# Revit family: Hager-UNIVERS-Surface_mounted-IP44-With_Cover-With_DIN-Hosted-PL-pl
name_source: partatom
category: Electrical Equipment
units: mm (PartAtom-declared; Revit-internal decimal feet)

## family parameters
Cut with Voids When Loaded = No
Host = Face
Maintain Annotation Orientation = Yes
Panel Configuration = Two Columns, Circuits Across
Part Type = Panelboard
Room Calculation Point = No
Round Connector Dimension = Use Diameter
Shared = No

## types (33) — shared parameters
BC_MODEL_ID = 1546917
BC_OBJECT_ID = 513407
BC_OBJECT_VERSION = #12
Code hager = ADD-EC000214_EU
EF000007 - Kolor = Biały
EF000024 - Odporność na promieniowanie UV = No
EF000049 - Głębokość = 165 mm  [stored 0.541339 ft]
EF000116 - Numer RAL = 9010
EF000118 - Z płytą montażową = No
EF000218 - Głębokość wbudowania = 161 mm  [stored 0.528215 ft]
EF001062 - Wykonanie zgodne z Dyrektywą Kompatybilności Elektromagnetycznej EMC = No
EF001088 - Możliwość rozbudowy = Yes
EF001134 - Szyna DIN = Yes
EF004462 - Rodzaj zamknięcia = Inne
EF005474 - Stopień ochrony (IP) = IP44
EF006244 - Transparentna pokrywa/drzwi = No
EF006306 - Z zamkiem = No
EF015941 - Drzwi przepuszczające sygnał = No
ETIM class code = EC000214
ETIM class name = Small distribution board
HG000002-with door or cover-pl = Yes
HG000003-Range-pl = UNIVERS
HG000005-Thickness-pl = 2 mm  [stored 0.00656168 ft]
HG000006-Flush mounted-pl = No
HG000011-Empty rows from bottom-pl = No
HG000012-Door swing angle-pl = 90.00°
HG000013-Door on the left-pl = No
HG000014-Door on the right-pl = Yes
HG000015-Clearance visibility-pl = Yes
HG000016-Door 3D visibility-pl = Yes
HG000017-Distance between poles-pl = 18 mm  [stored 0.0590551 ft]
HG000060-RAL-number = 9010
HG000099-Onfly Template ID-pl-PL = 507532
Manufacturer = Hager
Name = Hager-UNIVERS-Surface_mounted-IP44-With_Cover-With_DIN-NoHosted-PL-pl
Name BIM&CO = Electricity
Name hager = ADD_Enclosures_EC000214
Uniformat = Low Tension Service & Dist.
Uniformat code = D501001
zero-valued in all types: Default Elevation, EF001131 - Głębokość wewnętrzna, HG000007-Number of empty columns-pl

## per-type parameters (varying)
| type | BC_VARIANT_ID | EF000003 - Sposób montażu | EF000008 - Szerokość | EF000040 - Wysokość | EF000266 - Liczba rzędów | EF000332 - Wysokość wbudowania | EF000846 - Szerokość wbudowania | EF002950 - Szerokość wyrażona liczbą modułów | EF009212 - Wykonanie/rodzaj pokrywy | EF015776 - Listwa zaciskowa uziemienia | EF015777 - Listwa zaciskowa przewodu neutralnego | HG000001-Number of columns-pl | HG000004-Manufacturer reference-pl | HG000008-Number of empty rows-pl | HG000009-Double swing door-pl | HG000010-Asymmetric doors-pl | HGEF000266-Liczba rzędów | HGEF0002950-Szerokość wyrażona liczbą modułów |
| UNIVERS-Surface_mounted_W300_H500_D165_12_Modular_Spacing-FWB31S | 1173306 | Montaż natynkowy | 300 mm | 500 mm  [stored 1.64042 ft] | 3 | 500 mm  [stored 1.64042 ft] | 300 mm | 12 | Z otworem | Yes | Yes | 1 | FWB31S | 0 | No | No | 3 | 12 |
| UNIVERS-Surface_mounted_W550_H500_D165_26_Modular_Spacing-FWB32M2 | 1173307 | Montaż natynkowy | 550 mm | 500 mm  [stored 1.64042 ft] | 3 | 500 mm  [stored 1.64042 ft] | 550 mm | 26 | Zamknięty | No | No | 1 | FWB32M2 | 0 | No | No | 3 | 26 |
| UNIVERS-Surface_mounted_W550_H500_D165_24_Modular_Spacing-FWB32S | 1173308 | Montaż natynkowy | 550 mm | 500 mm  [stored 1.64042 ft] | 3 | 500 mm  [stored 1.64042 ft] | 550 mm | 24 | Z otworem | Yes | Yes | 2 | FWB32S | 0 | No | No | 3 | 24 |
| UNIVERS-Surface_mounted_W800_H500_D165_36_Modular_Spacing-FWB33S | 1173309 | Montaż natynkowy | 800 mm  [stored 2.62467 ft] | 500 mm  [stored 1.64042 ft] | 3 | 500 mm  [stored 1.64042 ft] | 800 mm  [stored 2.62467 ft] | 36 | Z otworem | Yes | Yes | 3 | FWB33S | 0 | Yes | Yes | 3 | 36 |
| UNIVERS-Surface_mounted_W1050_H500_D165_48_Modular_Spacing-FWB34S | 1173310 | Montaż natynkowy | 1050 mm | 500 mm  [stored 1.64042 ft] | 3 | 500 mm  [stored 1.64042 ft] | 1050 mm | 48 | Z otworem | Yes | Yes | 4 | FWB34S | 0 | Yes | No | 3 | 48 |
| UNIVERS-Surface_mounted_W300_H650_D165_12_Modular_Spacing-FWB41S | 1173311 | Montaż natynkowy | 300 mm | 650 mm  [stored 2.13255 ft] | 4 | 650 mm  [stored 2.13255 ft] | 300 mm | 12 | Z otworem | Yes | Yes | 1 | FWB41S | 0 | No | No | 4 | 12 |
| UNIVERS-Surface_mounted_W550_H650_D165_26_Modular_Spacing-FWB42M2 | 1173312 | Montaż natynkowy | 550 mm | 650 mm  [stored 2.13255 ft] | 4 | 650 mm  [stored 2.13255 ft] | 550 mm | 26 | Zamknięty | No | No | 1 | FWB42M2 | 0 | No | No | 4 | 26 |
| UNIVERS-Surface_mounted_W550_H650_D165_24_Modular_Spacing-FWB42S | 1173313 | Natynkowy/podtynkowy | 550 mm | 650 mm  [stored 2.13255 ft] | 4 | 650 mm  [stored 2.13255 ft] | 550 mm | 24 | Z otworem | Yes | Yes | 2 | FWB42S | 0 | No | No | 4 | 24 |
| UNIVERS-Surface_mounted_W800_H650_D165_36_Modular_Spacing-FWB43S | 1173314 | Montaż natynkowy | 800 mm  [stored 2.62467 ft] | 650 mm  [stored 2.13255 ft] | 4 | 650 mm  [stored 2.13255 ft] | 800 mm  [stored 2.62467 ft] | 36 | Z otworem | Yes | Yes | 3 | FWB43S | 0 | Yes | Yes | 4 | 36 |
| UNIVERS-Surface_mounted_W1050_H650_D165_48_Modular_Spacing-FWB44S | 1173315 | Montaż natynkowy | 1050 mm | 650 mm  [stored 2.13255 ft] | 4 | 650 mm  [stored 2.13255 ft] | 1050 mm | 48 | Z otworem | Yes | Yes | 4 | FWB44S | 0 | Yes | No | 4 | 48 |
| UNIVERS-Surface_mounted_W300_H800_D165_12_Modular_Spacing-FWB51S | 1173316 | Montaż natynkowy | 300 mm | 800 mm  [stored 2.62467 ft] | 5 | 800 mm  [stored 2.62467 ft] | 300 mm | 12 | Z otworem | Yes | Yes | 1 | FWB51S | 0 | No | No | 5 | 12 |
| UNIVERS-Surface_mounted_W550_H800_D165_26_Modular_Spacing-FWB52M2 | 1173317 | Montaż natynkowy | 550 mm | 800 mm  [stored 2.62467 ft] | 5 | 800 mm  [stored 2.62467 ft] | 550 mm | 26 | Zamknięty | No | No | 1 | FWB52M2 | 0 | No | No | 5 | 26 |
| UNIVERS-Surface_mounted_W550_H800_D165_24_Modular_Spacing-FWB52N | 1173318 | Montaż natynkowy | 550 mm | 800 mm  [stored 2.62467 ft] | 5 | 800 mm  [stored 2.62467 ft] | 550 mm | 24 | Z otworem | No | No | 2 | FWB52N | 2 | No | No | 5 | 24 |
| UNIVERS-Surface_mounted_W550_H800_D165_24_Modular_Spacing-FWB52S | 1173319 | Montaż natynkowy | 550 mm | 800 mm  [stored 2.62467 ft] | 5 | 800 mm  [stored 2.62467 ft] | 550 mm | 24 | Z otworem | Yes | Yes | 2 | FWB52S | 0 | No | No | 5 | 24 |
| UNIVERS-Surface_mounted_W800_H800_D165_36_Modular_Spacing-FWB53N | 1173320 | Montaż natynkowy | 800 mm  [stored 2.62467 ft] | 800 mm  [stored 2.62467 ft] | 5 | 800 mm  [stored 2.62467 ft] | 800 mm  [stored 2.62467 ft] | 36 | Z otworem | No | No | 3 | FWB53N | 2 | Yes | Yes | 5 | 36 |
| UNIVERS-Surface_mounted_W800_H800_D165_36_Modular_Spacing-FWB53S | 1173321 | Montaż natynkowy | 800 mm  [stored 2.62467 ft] | 800 mm  [stored 2.62467 ft] | 5 | 800 mm  [stored 2.62467 ft] | 800 mm  [stored 2.62467 ft] | 36 | Z otworem | Yes | Yes | 3 | FWB53S | 0 | Yes | Yes | 5 | 36 |
| UNIVERS-Surface_mounted_W1050_H800_D165_48_Modular_Spacing-FWB54S | 1173322 | Montaż natynkowy | 1050 mm | 800 mm  [stored 2.62467 ft] | 5 | 800 mm  [stored 2.62467 ft] | 1050 mm | 48 | Z otworem | Yes | Yes | 4 | FWB54S | 0 | Yes | No | 5 | 48 |
| UNIVERS-Surface_mounted_W300_H950_D165_12_Modular_Spacing-FWB61S | 1173323 | Montaż natynkowy | 300 mm | 950 mm  [stored 3.1168 ft] | 6 | 950 mm  [stored 3.1168 ft] | 300 mm | 12 | Z otworem | Yes | Yes | 1 | FWB61S | 0 | No | No | 6 | 12 |
| UNIVERS-Surface_mounted_W550_H950_D165_26_Modular_Spacing-FWB62M2 | 1173324 | Montaż natynkowy | 550 mm | 950 mm  [stored 3.1168 ft] | 6 | 950 mm  [stored 3.1168 ft] | 550 mm | 26 | Zamknięty | No | No | 1 | FWB62M2 | 0 | No | No | 6 | 26 |
| UNIVERS-Surface_mounted_W550_H950_D165_24_Modular_Spacing-FWB62N | 1173325 | Montaż natynkowy | 550 mm | 950 mm  [stored 3.1168 ft] | 6 | 950 mm  [stored 3.1168 ft] | 550 mm | 24 | Z otworem | No | No | 2 | FWB62N | 2 | No | No | 6 | 24 |
| UNIVERS-Surface_mounted_W550_H950_D165_24_Modular_Spacing-FWB62S | 1173326 | Montaż natynkowy | 550 mm | 950 mm  [stored 3.1168 ft] | 6 | 950 mm  [stored 3.1168 ft] | 550 mm | 24 | Z otworem | Yes | Yes | 2 | FWB62S | 0 | No | No | 6 | 24 |
| UNIVERS-Surface_mounted_W800_H950_D165_36_Modular_Spacing-FWB63N | 1173327 | Montaż natynkowy | 800 mm  [stored 2.62467 ft] | 950 mm  [stored 3.1168 ft] | 6 | 950 mm  [stored 3.1168 ft] | 800 mm  [stored 2.62467 ft] | 36 | Z otworem | No | No | 3 | FWB63N | 2 | Yes | Yes | 6 | 36 |
| UNIVERS-Surface_mounted_W800_H950_D165_36_Modular_Spacing-FWB63S | 1173328 | Montaż natynkowy | 800 mm  [stored 2.62467 ft] | 950 mm  [stored 3.1168 ft] | 6 | 950 mm  [stored 3.1168 ft] | 800 mm  [stored 2.62467 ft] | 36 | Z otworem | Yes | Yes | 3 | FWB63S | 0 | Yes | Yes | 6 | 36 |
| UNIVERS-Surface_mounted_W1050_H950_D165_48_Modular_Spacing-FWB64N | 1173329 | Montaż natynkowy | 1050 mm | 950 mm  [stored 3.1168 ft] | 6 | 950 mm  [stored 3.1168 ft] | 1050 mm | 48 | Z otworem | No | No | 4 | FWB64N | 2 | Yes | No | 6 | 48 |
| UNIVERS-Surface_mounted_W1050_H950_D165_48_Modular_Spacing-FWB64S | 1173330 | Montaż natynkowy | 1050 mm | 950 mm  [stored 3.1168 ft] | 6 | 950 mm  [stored 3.1168 ft] | 1050 mm | 48 | Z otworem | Yes | Yes | 4 | FWB64S | 0 | Yes | No | 6 | 48 |
| UNIVERS-Surface_mounted_W300_H1100_D165_12_Modular_Spacing-FWB71S | 1173331 | Montaż natynkowy | 300 mm | 1100 mm | 7 | 1100 mm | 300 mm | 12 | Z otworem | Yes | Yes | 1 | FWB71S | 0 | No | No | 7 | 12 |
| UNIVERS-Surface_mounted_W550_H1100_D165_26_Modular_Spacing-FWB72M2 | 1173332 | Montaż natynkowy | 550 mm | 1100 mm | 7 | 1100 mm | 550 mm | 26 | Zamknięty | No | No | 1 | FWB72M2 | 0 | No | No | 7 | 26 |
| UNIVERS-Surface_mounted_W550_H1100_D165_24_Modular_Spacing-FWB72N | 1173333 | Montaż natynkowy | 550 mm | 1100 mm | 7 | 1100 mm | 550 mm | 24 | Z otworem | No | No | 2 | FWB72N | 2 | No | No | 7 | 24 |
| UNIVERS-Surface_mounted_W550_H1100_D165_24_Modular_Spacing-FWB72S | 1173334 | Natynkowy/podtynkowy | 550 mm | 1100 mm | 7 | 1100 mm | 550 mm | 24 | Z otworem | Yes | Yes | 2 | FWB72S | 0 | No | No | 7 | 24 |
| UNIVERS-Surface_mounted_W800_H1100_D165_36_Modular_Spacing-FWB73N | 1173335 | Montaż natynkowy | 800 mm  [stored 2.62467 ft] | 1100 mm | 7 | 1100 mm | 800 mm  [stored 2.62467 ft] | 36 | Z otworem | No | No | 3 | FWB73N | 2 | Yes | Yes | 7 | 36 |
| UNIVERS-Surface_mounted_W800_H1100_D165_36_Modular_Spacing-FWB73S | 1173336 | Natynkowy/podtynkowy | 800 mm  [stored 2.62467 ft] | 1100 mm | 7 | 1100 mm | 800 mm  [stored 2.62467 ft] | 36 | Z otworem | Yes | Yes | 3 | FWB73S | 0 | Yes | Yes | 7 | 36 |
| UNIVERS-Surface_mounted_W1050_H1100_D165_48_Modular_Spacing-FWB74N | 1173337 | Montaż natynkowy | 1050 mm | 1100 mm | 7 | 1100 mm | 1050 mm | 48 | Z otworem | No | No | 4 | FWB74N | 2 | Yes | No | 7 | 48 |
| UNIVERS-Surface_mounted_W1050_H1100_D165_48_Modular_Spacing-FWB74S | 1173338 | Natynkowy/podtynkowy | 1050 mm | 1100 mm | 7 | 1100 mm | 1050 mm | 48 | Z otworem | Yes | Yes | 4 | FWB74S | 0 | Yes | No | 7 | 48 |

note: column(s) folded — value = type name in every type: Reference

note: [stored X ft] marks values corroborated as IEEE doubles in the binary element streams (Revit-internal decimal feet)

## geometry (parser evidence)
native form markers: Sweep x17
no freeform markers — native parametric forms only
